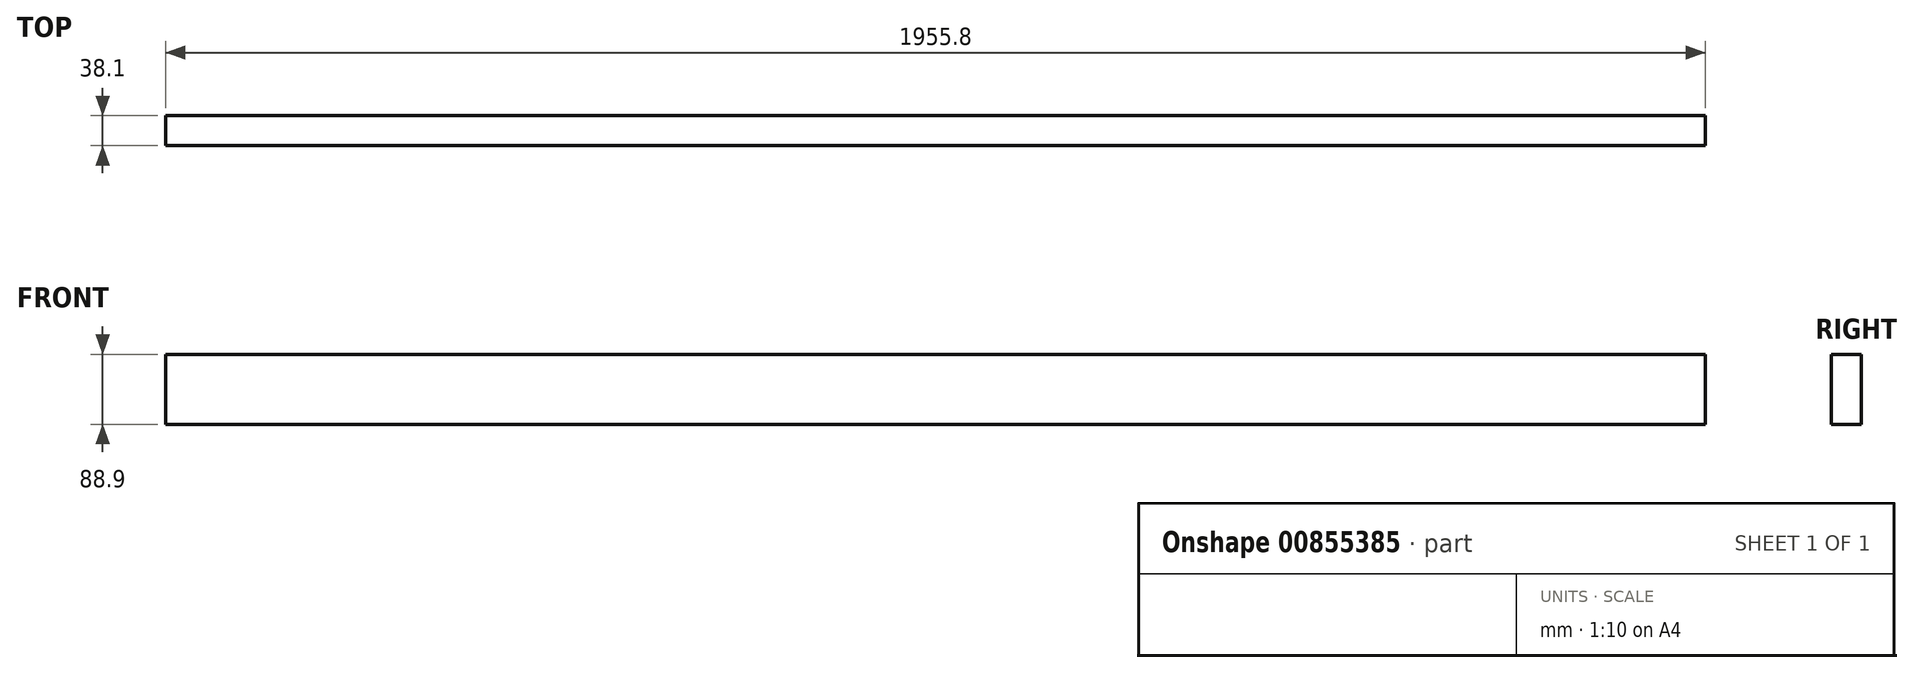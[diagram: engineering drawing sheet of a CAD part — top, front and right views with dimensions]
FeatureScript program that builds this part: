
annotation { "Feature Type Name" : "Feature", "Feature Type Description" : "" }
export const myFeature = defineFeature(function(context is Context, id is Id, definition is map)
    precondition{}
    {
        {
            var Q0;
            Q0=qCreatedBy(makeId("Right.planeOp"),FACE);
            var sketch = newSketch(context, id + "F0", { "sketchPlane" : qUnion([Q0])});
            skLineSegment(sketch, "E0.bottom", {"start": v(0, 0) * mm, "end": v(38.1, 0) * mm});
            skLineSegment(sketch, "E0.top", {"start": v(0, 88.9) * mm, "end": v(38.1, 88.9) * mm});
            skLineSegment(sketch, "E0.left", {"start": v(0, 0) * mm, "end": v(0, 88.9) * mm});
            skLineSegment(sketch, "E0.right", {"start": v(38.1, 0) * mm, "end": v(38.1, 88.9) * mm});
            skSolve(sketch);
        }
        {
            var Q0;
            Q0 = qSketchRegion(id + "F0", true);
            extrude(context, id + "F1", {"entities" : qUnion([Q0]), "depth" : 1955.8 * mm, "offsetDistance" : 25.4 * mm});
        }
    });
